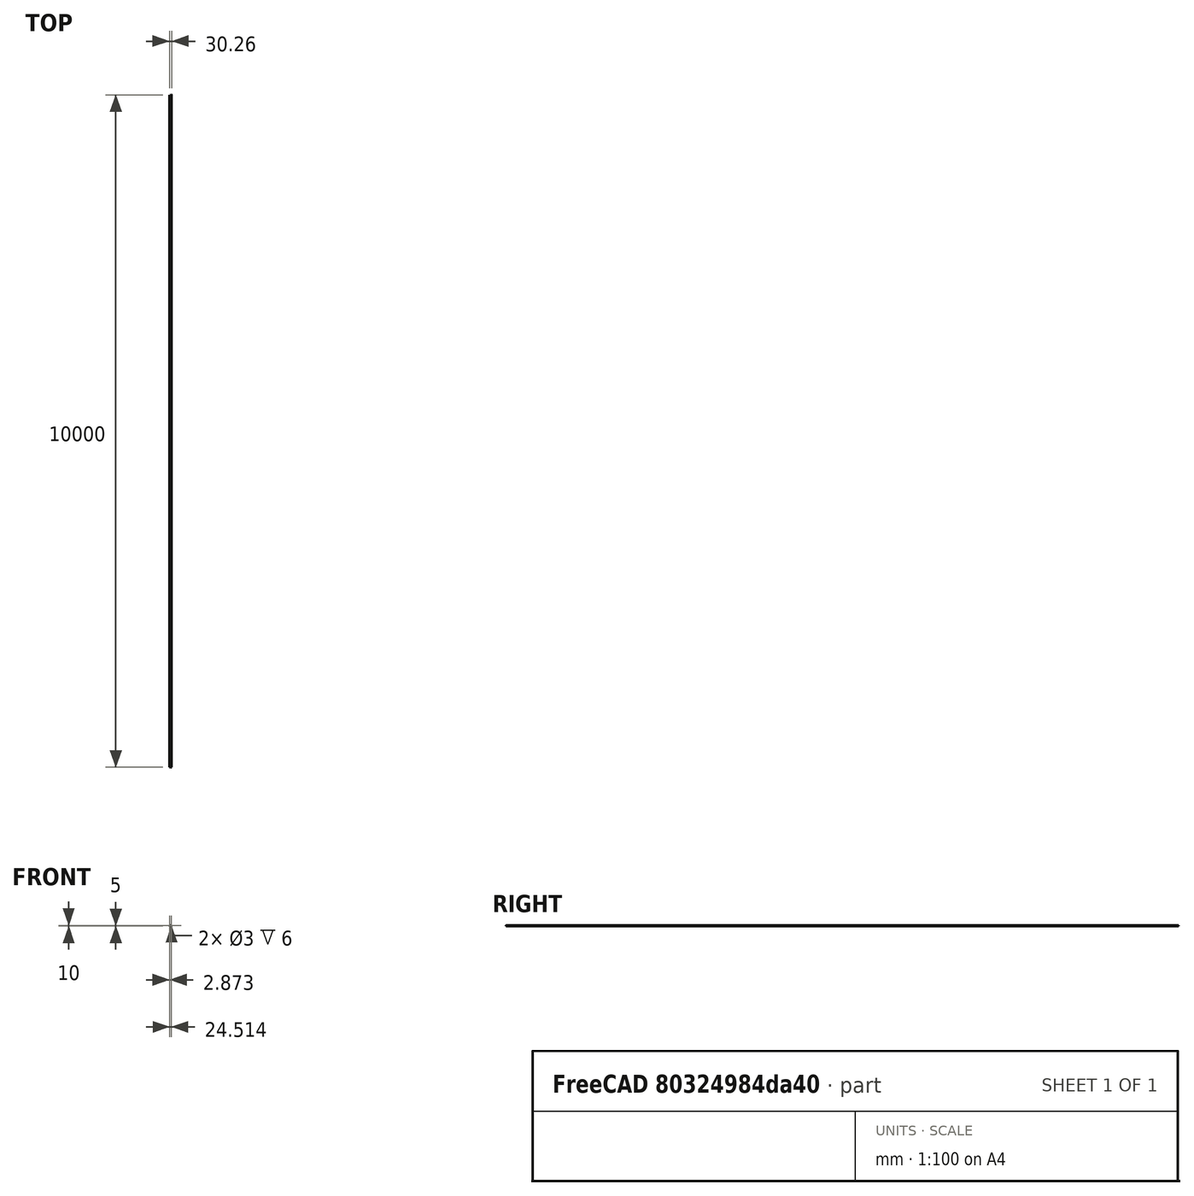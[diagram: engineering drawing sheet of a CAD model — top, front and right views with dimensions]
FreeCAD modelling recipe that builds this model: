
FCSTD DOCUMENT  (FreeCAD 0.16R)
Label: 10mmx35caps
License: All rights reserved
LicenseURL: http://en.wikipedia.org/wiki/All_rights_reserved
objects: Sketcher::SketchObject×3, PartDesign::Pocket×2, PartDesign::Fillet×2, PartDesign::Pad×1, PartDesign::Chamfer×1, Mesh::Feature×1
note: 12 computed .brp shape members not serialized (recipe doc carries the construction recipe); baked Part::Feature solids carry a one-line shape summary decoded from their .brp

FEATURE [Sketcher::SketchObject] Sketch
  sketch-geometry (8):
    g0: ArcOfCircle CenterX=0 CenterY=-2 CenterZ=0 NormalX=0 NormalY=0 NormalZ=1 Radius=14 StartAngle=0.608246 EndAngle=2.53335
    g1: ArcOfCircle CenterX=0 CenterY=-2 CenterZ=0 NormalX=0 NormalY=0 NormalZ=1 Radius=9.6 StartAngle=0.209871 EndAngle=2.93172
    g2: LineSegment StartX=-15.125 StartY=6 StartZ=0 EndX=-11.4891 EndY=6 EndZ=0
    g3: LineSegment StartX=15.125 StartY=6 StartZ=0 EndX=15.125 EndY=0 EndZ=0
    g4: LineSegment StartX=15.125 StartY=0 StartZ=0 EndX=9.38936 EndY=0 EndZ=0
    g5: LineSegment StartX=-15.125 StartY=6 StartZ=0 EndX=-15.125 EndY=0 EndZ=0
    g6: LineSegment StartX=-15.125 StartY=0 StartZ=0 EndX=-9.38936 EndY=0 EndZ=0
    g7: LineSegment StartX=11.4891 StartY=6 StartZ=0 EndX=15.125 EndY=6 EndZ=0
  constraints (27):
    c: PointOnObject(g0,g-2)
    c: DistanceY(g0) = -2
    c: PointOnObject(g1,g-2)
    c: Radius(g0) = 14
    c: Radius(g1) = 9.6
    c: PointOnObject(g1,g-1)
    c: PointOnObject(g1,g-1)
    c: Coincident(g1,g0)
    c: Horizontal(g2)
    c: Coincident(g7,g3)
    c: PointOnObject(g3,g-1)
    c: Coincident(g3,g4)
    c: Coincident(g4,g1)
    c: Coincident(g2,g5)
    c: PointOnObject(g5,g-1)
    c: Vertical(g5)
    c: Coincident(g5,g6)
    c: Horizontal(g6)
    c: Coincident(g1,g6)
    c: Vertical(g3)
    c: Symmetric(g7,g2,g-2)
    c: DistanceY(g3,g3) = 6
    c: PointOnObject(g0,g2)
    c: PointOnObject(g0,g2)
    c: Coincident(g7,g0)
    c: Coincident(g2,g0)
    c: DistanceX(g5,g3) = 30.25
FEATURE [PartDesign::Pad] Pad
  Length = 10
  Length2 = 100
  Sketch = -> Sketch
  Type = 0
FEATURE [Sketcher::SketchObject] Sketch001
  ExternalGeometry = -> [Pad]
  Placement = pos=(0,0,0) rot=(1,0,0;1.5708rad)
  Support = -> Pad [Face6]
  sketch-geometry (2):
    g0: Circle CenterX=-12.2572 CenterY=5 CenterZ=0 NormalX=0 NormalY=0 NormalZ=1 Radius=1.5
    g1: Circle CenterX=12.2572 CenterY=5 CenterZ=0 NormalX=0 NormalY=0 NormalZ=1 Radius=1.5
  constraints (4):
    c: Radius(g0) = 1.5
    c: Equal(g0,g1)
    c: Symmetric(g-5,g-6,g1)
    c: Symmetric(g-3,g-4,g0)
FEATURE [PartDesign::Pocket] Pocket
  Length = 5
  Sketch = -> Sketch001
  Type = 1
FEATURE [Sketcher::SketchObject] Sketch002
  ExternalGeometry = -> [Pocket]
  Placement = pos=(0,6,0) rot=(0,0.707107,0.707107;3.14159rad)
  Support = -> Pocket [Face3]
  sketch-geometry (2):
    g0: Circle CenterX=-12.2572 CenterY=5 CenterZ=0 NormalX=0 NormalY=0 NormalZ=1 Radius=3
    g1: Circle CenterX=12.2572 CenterY=5 CenterZ=0 NormalX=0 NormalY=0 NormalZ=1 Radius=3
  constraints (4):
    c: Radius(g0) = 3
    c: Coincident(g0,g-4)
    c: Radius(g1) = 3
    c: Coincident(g1,g-5)
FEATURE [PartDesign::Pocket] Pocket001
  Length = 13
  Reversed = true
  Sketch = -> Sketch002
  Type = 1
FEATURE [PartDesign::Chamfer] Chamfer
  Base = -> Pocket001 [Edge23,Edge21,Edge5,Edge28,Edge27,Edge15,Edge16,Edge1,Edge10,Edge11]
  Size = 1
FEATURE [PartDesign::Fillet] Fillet
  Base = -> Chamfer [Edge3,Edge8]
  Radius = 1
FEATURE [PartDesign::Fillet] Fillet001
  Base = -> Fillet [Edge23,Edge37]
  Radius = 0.5
FEATURE [Mesh::Feature] Mesh  label="Fillet001 (Meshed)"
